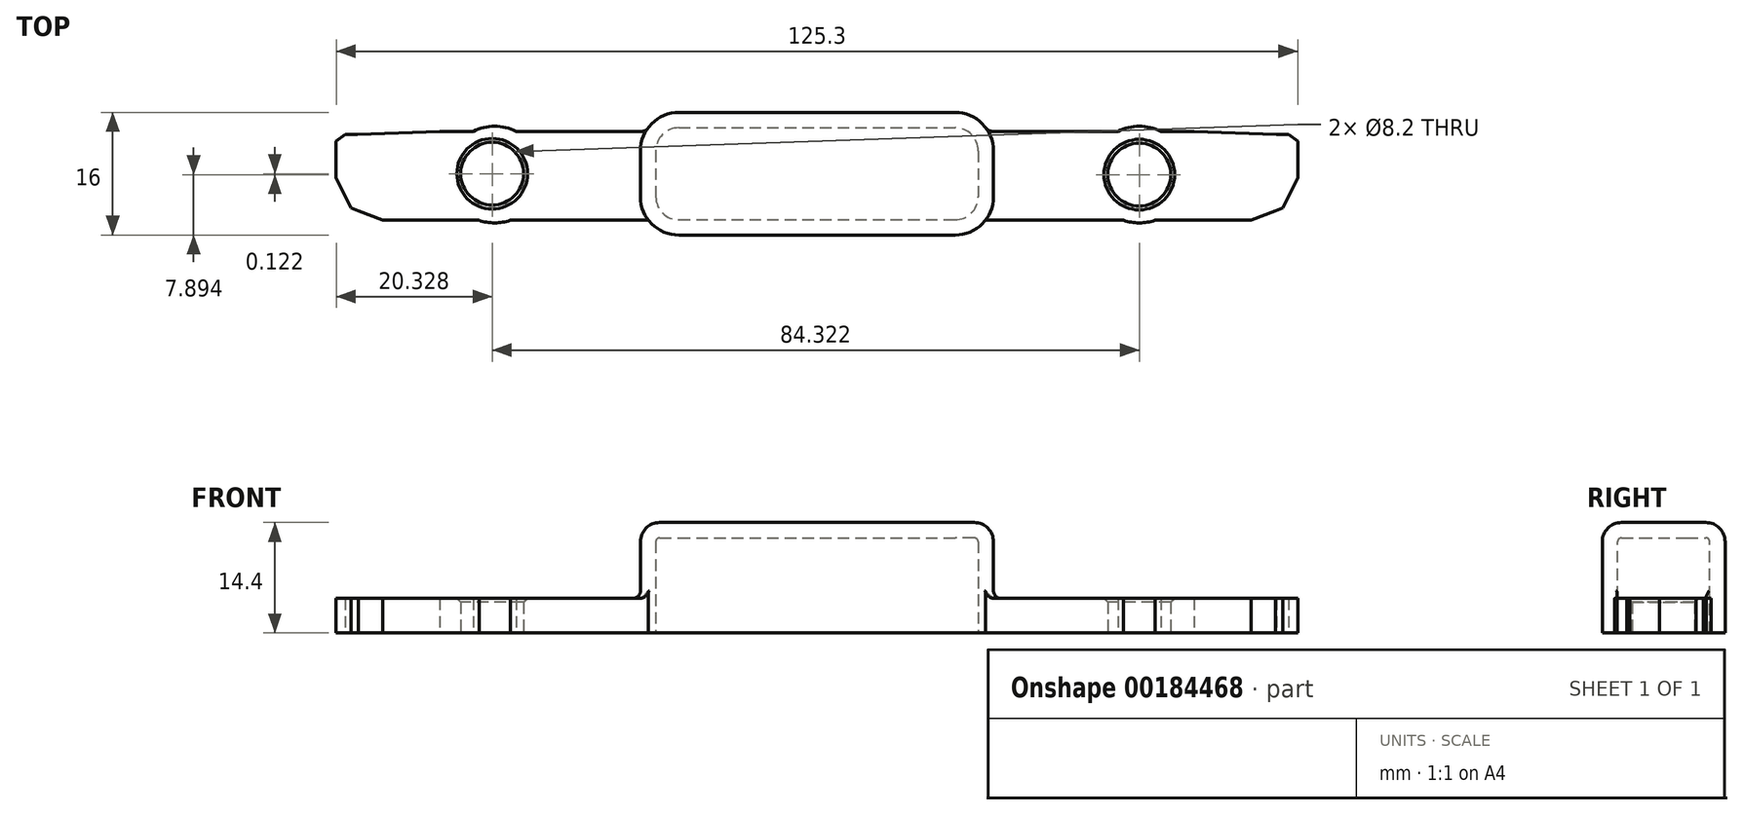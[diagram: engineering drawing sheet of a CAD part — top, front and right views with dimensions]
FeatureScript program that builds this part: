
annotation { "Feature Type Name" : "Feature", "Feature Type Description" : "" }
export const myFeature = defineFeature(function(context is Context, id is Id, definition is map)
    precondition{}
    {
        {
            var Q0;
            Q0=qCreatedBy(makeId("Top.planeOp"),FACE);
            var sketch = newSketch(context, id + "F0", { "sketchPlane" : qUnion([Q0])});
            skLineSegment(sketch, "E0.bottom", {"start": v(-18, 16) * mm, "end": v(18, 16) * mm});
            skLineSegment(sketch, "E0.top", {"start": v(-18, 0) * mm, "end": v(18, 0) * mm});
            skLineSegment(sketch, "E0.left", {"start": v(-23, 11) * mm, "end": v(-23, 5) * mm});
            skLineSegment(sketch, "E0.right", {"start": v(23, 11) * mm, "end": v(23, 5) * mm});
            skPoint(sketch, "E1.visualSharp", {"position": v(-23, 16) * mm});
            skArc(sketch, "E1.filletArc", {"start": v(-18, 16) * mm, "mid": v(-21.54, 14.54) * mm, "end": v(-23, 11) * mm});
            skPoint(sketch, "E2.visualSharp", {"position": v(-23, 0) * mm});
            skArc(sketch, "E2.filletArc", {"start": v(-23, 5) * mm, "mid": v(-21.54, 1.46) * mm, "end": v(-18, 0) * mm});
            skPoint(sketch, "E3.visualSharp", {"position": v(23, 0) * mm});
            skArc(sketch, "E3.filletArc", {"start": v(18, 0) * mm, "mid": v(21.54, 1.46) * mm, "end": v(23, 5) * mm});
            skPoint(sketch, "E4.visualSharp", {"position": v(23, 16) * mm});
            skArc(sketch, "E4.filletArc", {"start": v(23, 11) * mm, "mid": v(21.54, 14.54) * mm, "end": v(18, 16) * mm});
            skSolve(sketch);
        }
        {
            var Q0;
            Q0=makeQuery(id+"F0.imprint","IMPRINT",FACE,{"disambiguationData":[TD([[makeQuery(id+"F0.imprint","IMPRINT",EDGE,{"derivedFrom":sQuery(id+"F0.wireOp",EDGE,"E0.bottom")}),-1.0]])]});
            extrude(context, id + "F1", {"entities" : qUnion([Q0]), "depth" : 14.4 * mm});
        }
        {
            var Q0;
            Q0=makeQuery(id+"F1.opExtrude","CAP_FACE",FACE,{"disambiguationData":[OSD([sQuery(id+"F0.wireOp",EDGE,"E0.bottom"),sQuery(id+"F0.wireOp",EDGE,"E0.top"),sQuery(id+"F0.wireOp",EDGE,"E0.left"),sQuery(id+"F0.wireOp",EDGE,"E0.right"),sQuery(id+"F0.wireOp",EDGE,"E1.filletArc"),sQuery(id+"F0.wireOp",EDGE,"E2.filletArc"),sQuery(id+"F0.wireOp",EDGE,"E3.filletArc"),sQuery(id+"F0.wireOp",EDGE,"E4.filletArc")])],"isStart":false});
            fillet(context, id + "F2", {"entities" : qUnion([Q0]), "radius" : 2.5 * mm, "tangentPropagation" : true, "allowEdgeOverflow" : false});
        }
        {
            var Q0;
            Q0=makeQuery(id+"F1.opExtrude","CAP_FACE",FACE,{"disambiguationData":[OSD([sQuery(id+"F0.wireOp",EDGE,"E0.bottom"),sQuery(id+"F0.wireOp",EDGE,"E0.top"),sQuery(id+"F0.wireOp",EDGE,"E0.left"),sQuery(id+"F0.wireOp",EDGE,"E0.right"),sQuery(id+"F0.wireOp",EDGE,"E1.filletArc"),sQuery(id+"F0.wireOp",EDGE,"E2.filletArc"),sQuery(id+"F0.wireOp",EDGE,"E3.filletArc"),sQuery(id+"F0.wireOp",EDGE,"E4.filletArc")])],"isStart":true});
            shell(context, id + "F3", {"entities" : qUnion([Q0]), "thickness" : 2 * mm});
        }
        {
            var Q0;
            Q0=qCreatedBy(makeId("Top.planeOp"),FACE);
            var sketch = newSketch(context, id + "F4", { "sketchPlane" : qUnion([Q0])});
            skCircle(sketch, "E5", {"center": v(42, 7.9) * mm, "radius": 4.1 * mm});
            skCircle(sketch, "E6.0", {"center": v(42, 7.9) * mm, "radius": 6.3 * mm});
            skSolve(sketch);
        }
        {
            var Q0;
            Q0=makeQuery(id+"F4.imprint","IMPRINT",FACE,{"disambiguationData":[TD([[makeQuery(id+"F4.imprint","IMPRINT",EDGE,{"derivedFrom":sQuery(id+"F4.wireOp",EDGE,"E5")}),-1.0]])]});
            extrude(context, id + "F5", {"entities" : qUnion([Q0]), "depth" : 4.5 * mm});
        }
        {
            var Q0;
            Q0=makeQuery(id+"F5.opExtrude","SWEPT_BODY",BODY,{"disambiguationData":[OSD([sQuery(id+"F4.wireOp",EDGE,"E5"),sQuery(id+"F4.wireOp",EDGE,"E6.0")])]});
            var Q1;
            Q1=qCreatedBy(makeId("Right.planeOp"),FACE);
            mirror(context, id + "F6", {"entities" : qUnion([Q0]), "mirrorPlane" : qUnion([Q1])});
        }
        {
            var Q0;
            Q0=qCreatedBy(makeId("Top.planeOp"),FACE);
            var sketch = newSketch(context, id + "F7", { "sketchPlane" : qUnion([Q0])});
            skLineSegment(sketch, "E7", {"start": v(-22.21, 13.54) * mm, "end": v(-49.13, 13.54) * mm});
            skLineSegment(sketch, "E8", {"start": v(-49.13, 13.54) * mm, "end": v(-59.86, 13.15) * mm});
            skLineSegment(sketch, "E9", {"start": v(-59.86, 13.15) * mm, "end": v(-61.46, 13.15) * mm});
            skLineSegment(sketch, "E10", {"start": v(-61.46, 13.15) * mm, "end": v(-62.65, 12.24) * mm});
            skLineSegment(sketch, "E11", {"start": v(-62.65, 12.24) * mm, "end": v(-62.65, 7.45) * mm});
            skLineSegment(sketch, "E12", {"start": v(-62.65, 7.45) * mm, "end": v(-60.69, 3.57) * mm});
            skLineSegment(sketch, "E13", {"start": v(-60.69, 3.57) * mm, "end": v(-59.78, 3.17) * mm});
            skLineSegment(sketch, "E14", {"start": v(-59.78, 3.17) * mm, "end": v(-56.58, 1.93) * mm});
            skLineSegment(sketch, "E15", {"start": v(-56.58, 1.93) * mm, "end": v(-21.97, 1.93) * mm});
            skLineSegment(sketch, "E16", {"start": v(-21.97, 1.93) * mm, "end": v(-22.21, 13.54) * mm});
            skSolve(sketch);
        }
        {
            var Q0;
            Q0=makeQuery(id+"F7.imprint","IMPRINT",FACE,{"disambiguationData":[TD([[makeQuery(id+"F7.imprint","IMPRINT",EDGE,{"derivedFrom":sQuery(id+"F7.wireOp",EDGE,"E7")}),1.0]])]});
            extrude(context, id + "F8", {"entities" : qUnion([Q0]), "depth" : 4.5 * mm});
        }
        {
            var Q0;
            Q0=makeQuery(id+"F8.opExtrude","SWEPT_BODY",BODY,{"disambiguationData":[OSD([sQuery(id+"F7.wireOp",EDGE,"E7"),sQuery(id+"F7.wireOp",EDGE,"E8"),sQuery(id+"F7.wireOp",EDGE,"E9"),sQuery(id+"F7.wireOp",EDGE,"E10"),sQuery(id+"F7.wireOp",EDGE,"E11"),sQuery(id+"F7.wireOp",EDGE,"E12"),sQuery(id+"F7.wireOp",EDGE,"E13"),sQuery(id+"F7.wireOp",EDGE,"E14"),sQuery(id+"F7.wireOp",EDGE,"E15"),sQuery(id+"F7.wireOp",EDGE,"E16")])]});
            var Q1;
            Q1=qCreatedBy(makeId("Right.planeOp"),FACE);
            mirror(context, id + "F9", {"entities" : qUnion([Q0]), "mirrorPlane" : qUnion([Q1])});
        }
        {
            var Q0;
            Q0=makeQuery(id+"F1.opExtrude","SWEPT_BODY",BODY,{"disambiguationData":[OSD([sQuery(id+"F0.wireOp",EDGE,"E0.bottom"),sQuery(id+"F0.wireOp",EDGE,"E0.top"),sQuery(id+"F0.wireOp",EDGE,"E0.left"),sQuery(id+"F0.wireOp",EDGE,"E0.right"),sQuery(id+"F0.wireOp",EDGE,"E1.filletArc"),sQuery(id+"F0.wireOp",EDGE,"E2.filletArc"),sQuery(id+"F0.wireOp",EDGE,"E3.filletArc"),sQuery(id+"F0.wireOp",EDGE,"E4.filletArc")])]});
            var Q1;
            Q1=makeQuery(id+"F5.opExtrude","SWEPT_BODY",BODY,{"disambiguationData":[OSD([sQuery(id+"F4.wireOp",EDGE,"E5"),sQuery(id+"F4.wireOp",EDGE,"E6.0")])]});
            var Q2;
            Q2=makeQuery(id+"F6.opPattern","COPY",BODY,{"derivedFrom":makeQuery(id+"F5.opExtrude","SWEPT_BODY",BODY,{"disambiguationData":[OSD([sQuery(id+"F4.wireOp",EDGE,"E5"),sQuery(id+"F4.wireOp",EDGE,"E6.0")])]}),"instanceName":"1"});
            var Q3;
            Q3=makeQuery(id+"F8.opExtrude","SWEPT_BODY",BODY,{"disambiguationData":[OSD([sQuery(id+"F7.wireOp",EDGE,"E7"),sQuery(id+"F7.wireOp",EDGE,"E8"),sQuery(id+"F7.wireOp",EDGE,"E9"),sQuery(id+"F7.wireOp",EDGE,"E10"),sQuery(id+"F7.wireOp",EDGE,"E11"),sQuery(id+"F7.wireOp",EDGE,"E12"),sQuery(id+"F7.wireOp",EDGE,"E13"),sQuery(id+"F7.wireOp",EDGE,"E14"),sQuery(id+"F7.wireOp",EDGE,"E15"),sQuery(id+"F7.wireOp",EDGE,"E16")])]});
            var Q4;
            Q4=makeQuery(id+"F9.opPattern","COPY",BODY,{"derivedFrom":makeQuery(id+"F8.opExtrude","SWEPT_BODY",BODY,{"disambiguationData":[OSD([sQuery(id+"F7.wireOp",EDGE,"E7"),sQuery(id+"F7.wireOp",EDGE,"E8"),sQuery(id+"F7.wireOp",EDGE,"E9"),sQuery(id+"F7.wireOp",EDGE,"E10"),sQuery(id+"F7.wireOp",EDGE,"E11"),sQuery(id+"F7.wireOp",EDGE,"E12"),sQuery(id+"F7.wireOp",EDGE,"E13"),sQuery(id+"F7.wireOp",EDGE,"E14"),sQuery(id+"F7.wireOp",EDGE,"E15"),sQuery(id+"F7.wireOp",EDGE,"E16")])]}),"instanceName":"1"});
            var Q5;
            Q5=makeQuery(id+"FSgY8GwfA80SjcJ_3.opBoolean","INTERSECT",BODY,{"derivedFrom":[makeQuery(id+"F6.opPattern","COPY",BODY,{"derivedFrom":makeQuery(id+"F5.opExtrude","SWEPT_BODY",BODY,{"disambiguationData":[OSD([sQuery(id+"F4.wireOp",EDGE,"E5"),sQuery(id+"F4.wireOp",EDGE,"E6.0")])]}),"instanceName":"1"}),makeQuery(id+"F8.opExtrude","SWEPT_BODY",BODY,{"disambiguationData":[OSD([sQuery(id+"F7.wireOp",EDGE,"E7"),sQuery(id+"F7.wireOp",EDGE,"E8"),sQuery(id+"F7.wireOp",EDGE,"E9"),sQuery(id+"F7.wireOp",EDGE,"E10"),sQuery(id+"F7.wireOp",EDGE,"E11"),sQuery(id+"F7.wireOp",EDGE,"E12"),sQuery(id+"F7.wireOp",EDGE,"E13"),sQuery(id+"F7.wireOp",EDGE,"E14"),sQuery(id+"F7.wireOp",EDGE,"E15"),sQuery(id+"F7.wireOp",EDGE,"E16")])]})]});
            booleanBodies(context, id + "F10", {"operationType" : BooleanOperationType.UNION, "tools" : qUnion([Q0, Q1, Q2, Q3, Q4, Q5])});
        }
        {
            var Q0;
            Q0=qCreatedBy(makeId("Top.planeOp"),FACE);
            var sketch = newSketch(context, id + "F11", { "sketchPlane" : qUnion([Q0])});
            skCircle(sketch, "E17", {"center": v(42, 7.9) * mm, "radius": 4.1 * mm});
            skSolve(sketch);
        }
        {
            var Q0;
            Q0 = qSketchRegion(id + "F11", true);
            extrude(context, id + "F12", {"entities" : qUnion([Q0]), "operationType" : NewBodyOperationType.REMOVE, "depth" : 25 * mm});
        }
        {
            var Q0;
            Q0=qCreatedBy(makeId("Top.planeOp"),FACE);
            var sketch = newSketch(context, id + "F13", { "sketchPlane" : qUnion([Q0])});
            skCircle(sketch, "E18", {"center": v(-42.32, 8.02) * mm, "radius": 4.1 * mm});
            skSolve(sketch);
        }
        {
            var Q0;
            Q0 = qSketchRegion(id + "F13", true);
            extrude(context, id + "F14", {"entities" : qUnion([Q0]), "operationType" : NewBodyOperationType.REMOVE, "depth" : 25 * mm});
        }
        {
            var Q0;
            Q0=makeQuery(id+"F14.boolean.opBoolean","INTERSECT",EDGE,{"derivedFrom":[makeQuery(id+"F10.opBoolean","MERGE",FACE,{"derivedFrom":[makeQuery(id+"F6.opPattern","COPY",FACE,{"derivedFrom":makeQuery(id+"F5.opExtrude","CAP_FACE",FACE,{"disambiguationData":[OSD([sQuery(id+"F4.wireOp",EDGE,"E5"),sQuery(id+"F4.wireOp",EDGE,"E6.0")])],"isStart":false}),"instanceName":"1"}),makeQuery(id+"F8.opExtrude","CAP_FACE",FACE,{"disambiguationData":[OSD([sQuery(id+"F7.wireOp",EDGE,"E7"),sQuery(id+"F7.wireOp",EDGE,"E8"),sQuery(id+"F7.wireOp",EDGE,"E9"),sQuery(id+"F7.wireOp",EDGE,"E10"),sQuery(id+"F7.wireOp",EDGE,"E11"),sQuery(id+"F7.wireOp",EDGE,"E12"),sQuery(id+"F7.wireOp",EDGE,"E13"),sQuery(id+"F7.wireOp",EDGE,"E14"),sQuery(id+"F7.wireOp",EDGE,"E15"),sQuery(id+"F7.wireOp",EDGE,"E16")])],"isStart":false})]}),makeQuery(id+"F14.opExtrude","SWEPT_FACE",FACE,{"disambiguationData":[OSD([sQuery(id+"F13.wireOp",EDGE,"E18")])]})]});
            var Q1;
            Q1=makeQuery(id+"F12.boolean.opBoolean","INTERSECT",EDGE,{"derivedFrom":[makeQuery(id+"F10.opBoolean","MERGE",FACE,{"derivedFrom":[makeQuery(id+"F5.opExtrude","CAP_FACE",FACE,{"disambiguationData":[OSD([sQuery(id+"F4.wireOp",EDGE,"E5"),sQuery(id+"F4.wireOp",EDGE,"E6.0")])],"isStart":false}),makeQuery(id+"F9.opPattern","COPY",FACE,{"derivedFrom":makeQuery(id+"F8.opExtrude","CAP_FACE",FACE,{"disambiguationData":[OSD([sQuery(id+"F7.wireOp",EDGE,"E7"),sQuery(id+"F7.wireOp",EDGE,"E8"),sQuery(id+"F7.wireOp",EDGE,"E9"),sQuery(id+"F7.wireOp",EDGE,"E10"),sQuery(id+"F7.wireOp",EDGE,"E11"),sQuery(id+"F7.wireOp",EDGE,"E12"),sQuery(id+"F7.wireOp",EDGE,"E13"),sQuery(id+"F7.wireOp",EDGE,"E14"),sQuery(id+"F7.wireOp",EDGE,"E15"),sQuery(id+"F7.wireOp",EDGE,"E16")])],"isStart":false}),"instanceName":"1"})]}),makeQuery(id+"F12.opExtrude","SWEPT_FACE",FACE,{"disambiguationData":[OSD([sQuery(id+"F11.wireOp",EDGE,"E17")])]})]});
            chamfer(context, id + "F15", {"entities" : qUnion([Q0, Q1]), "width" : .5 * mm, "tangentPropagation" : true});
        }
        {
            var Q0;
            Q0=makeQuery(id+"F10.opBoolean","INTERSECT",EDGE,{"derivedFrom":[makeQuery(id+"F1.opExtrude","SWEPT_FACE",FACE,{"disambiguationData":[OSD([sQuery(id+"F0.wireOp",EDGE,"E2.filletArc")])]}),makeQuery(id+"F8.opExtrude","CAP_FACE",FACE,{"disambiguationData":[OSD([sQuery(id+"F7.wireOp",EDGE,"E7"),sQuery(id+"F7.wireOp",EDGE,"E8"),sQuery(id+"F7.wireOp",EDGE,"E9"),sQuery(id+"F7.wireOp",EDGE,"E10"),sQuery(id+"F7.wireOp",EDGE,"E11"),sQuery(id+"F7.wireOp",EDGE,"E12"),sQuery(id+"F7.wireOp",EDGE,"E13"),sQuery(id+"F7.wireOp",EDGE,"E14"),sQuery(id+"F7.wireOp",EDGE,"E15"),sQuery(id+"F7.wireOp",EDGE,"E16")])],"isStart":false})]});
            var Q1;
            Q1=makeQuery(id+"F10.opBoolean","INTERSECT",EDGE,{"derivedFrom":[makeQuery(id+"F1.opExtrude","SWEPT_FACE",FACE,{"disambiguationData":[OSD([sQuery(id+"F0.wireOp",EDGE,"E0.left")])]}),makeQuery(id+"F8.opExtrude","CAP_FACE",FACE,{"disambiguationData":[OSD([sQuery(id+"F7.wireOp",EDGE,"E7"),sQuery(id+"F7.wireOp",EDGE,"E8"),sQuery(id+"F7.wireOp",EDGE,"E9"),sQuery(id+"F7.wireOp",EDGE,"E10"),sQuery(id+"F7.wireOp",EDGE,"E11"),sQuery(id+"F7.wireOp",EDGE,"E12"),sQuery(id+"F7.wireOp",EDGE,"E13"),sQuery(id+"F7.wireOp",EDGE,"E14"),sQuery(id+"F7.wireOp",EDGE,"E15"),sQuery(id+"F7.wireOp",EDGE,"E16")])],"isStart":false})]});
            var Q2;
            Q2=makeQuery(id+"F10.opBoolean","INTERSECT",EDGE,{"derivedFrom":[makeQuery(id+"F1.opExtrude","SWEPT_FACE",FACE,{"disambiguationData":[OSD([sQuery(id+"F0.wireOp",EDGE,"E1.filletArc")])]}),makeQuery(id+"F8.opExtrude","CAP_FACE",FACE,{"disambiguationData":[OSD([sQuery(id+"F7.wireOp",EDGE,"E7"),sQuery(id+"F7.wireOp",EDGE,"E8"),sQuery(id+"F7.wireOp",EDGE,"E9"),sQuery(id+"F7.wireOp",EDGE,"E10"),sQuery(id+"F7.wireOp",EDGE,"E11"),sQuery(id+"F7.wireOp",EDGE,"E12"),sQuery(id+"F7.wireOp",EDGE,"E13"),sQuery(id+"F7.wireOp",EDGE,"E14"),sQuery(id+"F7.wireOp",EDGE,"E15"),sQuery(id+"F7.wireOp",EDGE,"E16")])],"isStart":false})]});
            var Q3;
            {var subQ0=sQuery(id+"F7.wireOp",EDGE,"E15");var subQ1=sQuery(id+"F7.wireOp",EDGE,"E16");Q3=makeQuery(id+"FtTYDY9AlvOJCH4_1.opFillet","BLEND_EDGE",EDGE,{"blendedFrom":[makeQuery(id+"F10.opBoolean","SPLIT",EDGE,{"disambiguationData":[TD([makeQuery(id+"F8.opExtrude","SWEPT_FACE",FACE,{"disambiguationData":[OSD([subQ1])]})])],"derivedFrom":makeQuery(id+"F8.opExtrude","CAP_EDGE",EDGE,{"disambiguationData":[OSD([subQ0])],"isStart":false})}),makeQuery(id+"F1.opExtrude","SWEPT_FACE",FACE,{"disambiguationData":[OSD([sQuery(id+"F0.wireOp",EDGE,"E2.filletArc")])]})],"blendedInto":[makeQuery(id+"F1.opExtrude","SWEPT_FACE",FACE,{"disambiguationData":[OSD([sQuery(id+"F0.wireOp",EDGE,"E2.filletArc")])]})]});}
            var Q4;
            {var subQ0=makeQuery(id+"F1.opExtrude","SWEPT_FACE",FACE,{"disambiguationData":[OSD([sQuery(id+"F0.wireOp",EDGE,"E1.filletArc")])]});var subQ1=sQuery(id+"F7.wireOp",EDGE,"E7");Q4=makeQuery(id+"FtTYDY9AlvOJCH4_1.opFillet","BLEND_EDGE",EDGE,{"blendedFrom":[makeQuery(id+"F10.opBoolean","SPLIT",EDGE,{"disambiguationData":[TD([subQ0])],"derivedFrom":makeQuery(id+"F8.opExtrude","CAP_EDGE",EDGE,{"disambiguationData":[OSD([subQ1])],"isStart":false})}),subQ0],"blendedInto":[subQ0]});}
            var Q5;
            Q5=makeQuery(id+"F10.opBoolean","INTERSECT",EDGE,{"derivedFrom":[makeQuery(id+"F1.opExtrude","SWEPT_FACE",FACE,{"disambiguationData":[OSD([sQuery(id+"F0.wireOp",EDGE,"E2.filletArc")])]}),makeQuery(id+"F8.opExtrude","SWEPT_FACE",FACE,{"disambiguationData":[OSD([sQuery(id+"F7.wireOp",EDGE,"E16")])]})]});
            var Q6;
            Q6=makeQuery(id+"F10.opBoolean","INTERSECT",EDGE,{"derivedFrom":[makeQuery(id+"F1.opExtrude","SWEPT_FACE",FACE,{"disambiguationData":[OSD([sQuery(id+"F0.wireOp",EDGE,"E1.filletArc")])]}),makeQuery(id+"F8.opExtrude","SWEPT_FACE",FACE,{"disambiguationData":[OSD([sQuery(id+"F7.wireOp",EDGE,"E7")])]})]});
            fillet(context, id + "F16", {"entities" : qUnion([Q0, Q1, Q2, Q3, Q4, Q5, Q6]), "radius" : 1 * mm, "tangentPropagation" : true, "allowEdgeOverflow" : false});
        }
        {
            var Q0;
            Q0=makeQuery(id+"F10.opBoolean","INTERSECT",EDGE,{"derivedFrom":[makeQuery(id+"F1.opExtrude","SWEPT_FACE",FACE,{"disambiguationData":[OSD([sQuery(id+"F0.wireOp",EDGE,"E0.right")])]}),makeQuery(id+"F9.opPattern","COPY",FACE,{"derivedFrom":makeQuery(id+"F8.opExtrude","CAP_FACE",FACE,{"disambiguationData":[OSD([sQuery(id+"F7.wireOp",EDGE,"E7"),sQuery(id+"F7.wireOp",EDGE,"E8"),sQuery(id+"F7.wireOp",EDGE,"E9"),sQuery(id+"F7.wireOp",EDGE,"E10"),sQuery(id+"F7.wireOp",EDGE,"E11"),sQuery(id+"F7.wireOp",EDGE,"E12"),sQuery(id+"F7.wireOp",EDGE,"E13"),sQuery(id+"F7.wireOp",EDGE,"E14"),sQuery(id+"F7.wireOp",EDGE,"E15"),sQuery(id+"F7.wireOp",EDGE,"E16")])],"isStart":false}),"instanceName":"1"})]});
            var Q1;
            Q1=makeQuery(id+"F10.opBoolean","INTERSECT",EDGE,{"derivedFrom":[makeQuery(id+"F1.opExtrude","SWEPT_FACE",FACE,{"disambiguationData":[OSD([sQuery(id+"F0.wireOp",EDGE,"E4.filletArc")])]}),makeQuery(id+"F9.opPattern","COPY",FACE,{"derivedFrom":makeQuery(id+"F8.opExtrude","SWEPT_FACE",FACE,{"disambiguationData":[OSD([sQuery(id+"F7.wireOp",EDGE,"E7")])]}),"instanceName":"1"})]});
            var Q2;
            Q2=makeQuery(id+"F10.opBoolean","INTERSECT",EDGE,{"derivedFrom":[makeQuery(id+"F1.opExtrude","SWEPT_FACE",FACE,{"disambiguationData":[OSD([sQuery(id+"F0.wireOp",EDGE,"E4.filletArc")])]}),makeQuery(id+"F9.opPattern","COPY",FACE,{"derivedFrom":makeQuery(id+"F8.opExtrude","CAP_FACE",FACE,{"disambiguationData":[OSD([sQuery(id+"F7.wireOp",EDGE,"E7"),sQuery(id+"F7.wireOp",EDGE,"E8"),sQuery(id+"F7.wireOp",EDGE,"E9"),sQuery(id+"F7.wireOp",EDGE,"E10"),sQuery(id+"F7.wireOp",EDGE,"E11"),sQuery(id+"F7.wireOp",EDGE,"E12"),sQuery(id+"F7.wireOp",EDGE,"E13"),sQuery(id+"F7.wireOp",EDGE,"E14"),sQuery(id+"F7.wireOp",EDGE,"E15"),sQuery(id+"F7.wireOp",EDGE,"E16")])],"isStart":false}),"instanceName":"1"})]});
            var Q3;
            {var subQ0=makeQuery(id+"F1.opExtrude","SWEPT_FACE",FACE,{"disambiguationData":[OSD([sQuery(id+"F0.wireOp",EDGE,"E4.filletArc")])]});var subQ1=sQuery(id+"F7.wireOp",EDGE,"E7");Q3=makeQuery(id+"FtTYDY9AlvOJCH4_1.opFillet","BLEND_EDGE",EDGE,{"blendedFrom":[makeQuery(id+"F10.opBoolean","SPLIT",EDGE,{"disambiguationData":[TD([subQ0])],"derivedFrom":makeQuery(id+"F9.opPattern","COPY",EDGE,{"derivedFrom":makeQuery(id+"F8.opExtrude","CAP_EDGE",EDGE,{"disambiguationData":[OSD([subQ1])],"isStart":false}),"instanceName":"1"})}),subQ0],"blendedInto":[subQ0]});}
            var Q4;
            Q4=makeQuery(id+"F10.opBoolean","INTERSECT",EDGE,{"derivedFrom":[makeQuery(id+"F1.opExtrude","SWEPT_FACE",FACE,{"disambiguationData":[OSD([sQuery(id+"F0.wireOp",EDGE,"E3.filletArc")])]}),makeQuery(id+"F9.opPattern","COPY",FACE,{"derivedFrom":makeQuery(id+"F8.opExtrude","CAP_FACE",FACE,{"disambiguationData":[OSD([sQuery(id+"F7.wireOp",EDGE,"E7"),sQuery(id+"F7.wireOp",EDGE,"E8"),sQuery(id+"F7.wireOp",EDGE,"E9"),sQuery(id+"F7.wireOp",EDGE,"E10"),sQuery(id+"F7.wireOp",EDGE,"E11"),sQuery(id+"F7.wireOp",EDGE,"E12"),sQuery(id+"F7.wireOp",EDGE,"E13"),sQuery(id+"F7.wireOp",EDGE,"E14"),sQuery(id+"F7.wireOp",EDGE,"E15"),sQuery(id+"F7.wireOp",EDGE,"E16")])],"isStart":false}),"instanceName":"1"})]});
            var Q5;
            {var subQ0=sQuery(id+"F7.wireOp",EDGE,"E15");var subQ2=sQuery(id+"F7.wireOp",EDGE,"E16");Q5=makeQuery(id+"FtTYDY9AlvOJCH4_1.opFillet","BLEND_EDGE",EDGE,{"blendedFrom":[makeQuery(id+"F10.opBoolean","SPLIT",EDGE,{"disambiguationData":[TD([makeQuery(id+"F9.opPattern","COPY",FACE,{"derivedFrom":makeQuery(id+"F8.opExtrude","SWEPT_FACE",FACE,{"disambiguationData":[OSD([subQ2])]}),"instanceName":"1"})])],"derivedFrom":makeQuery(id+"F9.opPattern","COPY",EDGE,{"derivedFrom":makeQuery(id+"F8.opExtrude","CAP_EDGE",EDGE,{"disambiguationData":[OSD([subQ0])],"isStart":false}),"instanceName":"1"})}),makeQuery(id+"F1.opExtrude","SWEPT_FACE",FACE,{"disambiguationData":[OSD([sQuery(id+"F0.wireOp",EDGE,"E3.filletArc")])]})],"blendedInto":[makeQuery(id+"F1.opExtrude","SWEPT_FACE",FACE,{"disambiguationData":[OSD([sQuery(id+"F0.wireOp",EDGE,"E3.filletArc")])]})]});}
            var Q6;
            Q6=makeQuery(id+"F10.opBoolean","INTERSECT",EDGE,{"derivedFrom":[makeQuery(id+"F1.opExtrude","SWEPT_FACE",FACE,{"disambiguationData":[OSD([sQuery(id+"F0.wireOp",EDGE,"E3.filletArc")])]}),makeQuery(id+"F9.opPattern","COPY",FACE,{"derivedFrom":makeQuery(id+"F8.opExtrude","SWEPT_FACE",FACE,{"disambiguationData":[OSD([sQuery(id+"F7.wireOp",EDGE,"E16")])]}),"instanceName":"1"})]});
            fillet(context, id + "F17", {"entities" : qUnion([Q0, Q1, Q2, Q3, Q4, Q5, Q6]), "radius" : 1 * mm, "tangentPropagation" : true, "allowEdgeOverflow" : false});
        }
    });
